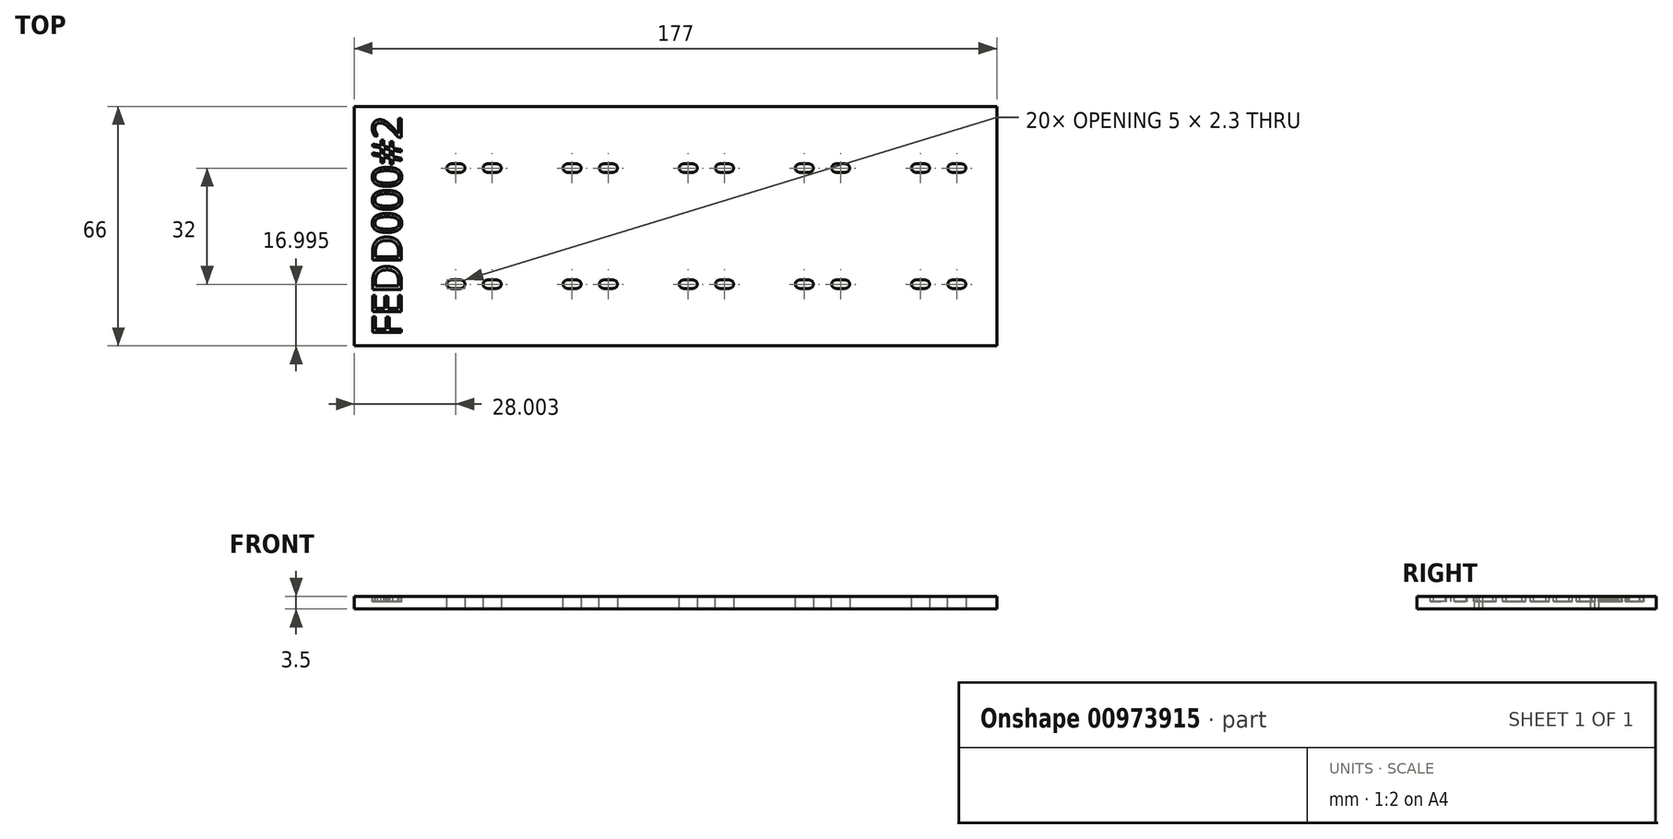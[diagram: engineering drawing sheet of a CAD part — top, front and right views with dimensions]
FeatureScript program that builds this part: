
annotation { "Feature Type Name" : "Feature", "Feature Type Description" : "" }
export const myFeature = defineFeature(function(context is Context, id is Id, definition is map)
    precondition{}
    {
        {
            var Q0;
            Q0=qCreatedBy(makeId("Top.planeOp"),FACE);
            var sketch = newSketch(context, id + "F0", { "sketchPlane" : qUnion([Q0])});
            skLineSegment(sketch, "E0.bottom", {"start": v(-87.55, 16.72) * mm, "end": v(89.45, 16.72) * mm});
            skLineSegment(sketch, "E0.top", {"start": v(-87.55, -49.28) * mm, "end": v(89.45, -49.28) * mm});
            skLineSegment(sketch, "E0.left", {"start": v(-87.55, 16.72) * mm, "end": v(-87.55, -49.28) * mm});
            skLineSegment(sketch, "E0.right", {"start": v(89.45, 16.72) * mm, "end": v(89.45, -49.28) * mm});
            skSolve(sketch);
        }
        {
            var Q0;
            Q0=makeQuery(id+"F0.imprint","IMPRINT",FACE,{"disambiguationData":[TD([[makeQuery(id+"F0.imprint","IMPRINT",EDGE,{"derivedFrom":sQuery(id+"F0.wireOp",EDGE,"E0.bottom")}),-1.0]])]});
            extrude(context, id + "F1", {"entities" : qUnion([Q0]), "depth" : 3.5 * mm, "offsetDistance" : 25 * mm});
        }
        {
            var Q0;
            Q0=makeQuery(id+"F1.opExtrude","CAP_FACE",FACE,{"disambiguationData":[OSD([sQuery(id+"F0.wireOp",EDGE,"E0.bottom"),sQuery(id+"F0.wireOp",EDGE,"E0.top"),sQuery(id+"F0.wireOp",EDGE,"E0.left"),sQuery(id+"F0.wireOp",EDGE,"E0.right")])],"isStart":false});
            var sketch = newSketch(context, id + "F2", { "sketchPlane" : qUnion([Q0])});
            skText(sketch, "E1", { "text": "FEDD000#2", "fontName": "OpenSans-Regular.ttf"});
            const initialGuessF2  = {"E1": [-0.07455, -0.0467, 0, 1, 0.008]};
            skSetInitialGuess(sketch, initialGuessF2);
            skSolve(sketch);
        }
        {
            var Q0;
            Q0=qSketchRegion(id+"F2",true);
            extrude(context, id + "F3", {"entities" : qUnion([Q0]), "operationType" : NewBodyOperationType.REMOVE, "oppositeDirection" : true, "depth" : 1.5 * mm, "offsetDistance" : 25 * mm});
        }
        {
            var Q0;
            {var subQ0=sQuery(id+"F0.wireOp",EDGE,"E0.left");var subQ1=sQuery(id+"F0.wireOp",EDGE,"E0.bottom");var subQ2=sQuery(id+"F0.wireOp",EDGE,"E0.right");var subQ3=sQuery(id+"F0.wireOp",EDGE,"E0.top");Q0=makeQuery(id+"F3.boolean.opBoolean","SPLIT",FACE,{"disambiguationData":[TD([makeQuery(id+"F1.opExtrude","SWEPT_FACE",FACE,{"disambiguationData":[OSD([subQ1])]})])],"derivedFrom":makeQuery(id+"F1.opExtrude","CAP_FACE",FACE,{"disambiguationData":[OSD([subQ1,subQ3,subQ0,subQ2])],"isStart":false})});}
            var sketch = newSketch(context, id + "F4", { "sketchPlane" : qUnion([Q0])});
            skCircle(sketch, "E2", {"center": v(-59.55, -0.28) * mm, "radius": 1.15 * mm});
            skCircle(sketch, "E3", {"center": v(-49.55, -0.28) * mm, "radius": 1.15 * mm});
            skCircle(sketch, "E4", {"center": v(-27.55, -0.28) * mm, "radius": 1.15 * mm});
            skCircle(sketch, "E5", {"center": v(-17.55, -0.28) * mm, "radius": 1.15 * mm});
            skCircle(sketch, "E6", {"center": v(4.45, -0.28) * mm, "radius": 1.15 * mm});
            skCircle(sketch, "E7", {"center": v(14.45, -0.28) * mm, "radius": 1.15 * mm});
            skCircle(sketch, "E8", {"center": v(36.45, -0.28) * mm, "radius": 1.15 * mm});
            skCircle(sketch, "E9", {"center": v(46.45, -0.28) * mm, "radius": 1.15 * mm});
            skCircle(sketch, "E10", {"center": v(68.45, -0.28) * mm, "radius": 1.15 * mm});
            skCircle(sketch, "E11", {"center": v(78.45, -0.28) * mm, "radius": 1.15 * mm});
            skCircle(sketch, "E12", {"center": v(-59.55, -32.28) * mm, "radius": 1.15 * mm});
            skCircle(sketch, "E13", {"center": v(-49.55, -32.28) * mm, "radius": 1.15 * mm});
            skCircle(sketch, "E14", {"center": v(-27.55, -32.28) * mm, "radius": 1.15 * mm});
            skCircle(sketch, "E15", {"center": v(-17.55, -32.28) * mm, "radius": 1.15 * mm});
            skCircle(sketch, "E16", {"center": v(4.45, -32.28) * mm, "radius": 1.15 * mm});
            skCircle(sketch, "E17", {"center": v(14.45, -32.28) * mm, "radius": 1.15 * mm});
            skCircle(sketch, "E18", {"center": v(36.45, -32.28) * mm, "radius": 1.15 * mm});
            skCircle(sketch, "E19", {"center": v(46.45, -32.28) * mm, "radius": 1.15 * mm});
            skCircle(sketch, "E20", {"center": v(68.45, -32.28) * mm, "radius": 1.15 * mm});
            skCircle(sketch, "E21", {"center": v(78.45, -32.28) * mm, "radius": 1.15 * mm});
            skLineSegment(sketch, "E22.bottom", {"start": v(-62.05, -31.13) * mm, "end": v(-57.05, -31.13) * mm});
            skLineSegment(sketch, "E22.top", {"start": v(-62.05, -33.43) * mm, "end": v(-57.05, -33.43) * mm});
            skLineSegment(sketch, "E22.left", {"start": v(-62.05, -31.13) * mm, "end": v(-62.05, -33.43) * mm});
            skLineSegment(sketch, "E22.right", {"start": v(-57.05, -31.13) * mm, "end": v(-57.05, -33.43) * mm});
            skLineSegment(sketch, "E23.bottom", {"start": v(-62.05, 0.87) * mm, "end": v(-57.05, 0.87) * mm});
            skLineSegment(sketch, "E23.top", {"start": v(-62.05, -1.43) * mm, "end": v(-57.05, -1.43) * mm});
            skLineSegment(sketch, "E23.left", {"start": v(-62.05, 0.87) * mm, "end": v(-62.05, -1.43) * mm});
            skLineSegment(sketch, "E23.right", {"start": v(-57.05, 0.87) * mm, "end": v(-57.05, -1.43) * mm});
            skLineSegment(sketch, "E24.bottom", {"start": v(-52.05, 0.87) * mm, "end": v(-47.05, 0.87) * mm});
            skLineSegment(sketch, "E24.top", {"start": v(-52.05, -1.43) * mm, "end": v(-47.05, -1.43) * mm});
            skLineSegment(sketch, "E24.left", {"start": v(-52.05, 0.87) * mm, "end": v(-52.05, -1.43) * mm});
            skLineSegment(sketch, "E24.right", {"start": v(-47.05, 0.87) * mm, "end": v(-47.05, -1.43) * mm});
            skLineSegment(sketch, "E25.bottom", {"start": v(-30.05, 0.87) * mm, "end": v(-25.05, 0.87) * mm});
            skLineSegment(sketch, "E25.top", {"start": v(-30.05, -1.43) * mm, "end": v(-25.05, -1.43) * mm});
            skLineSegment(sketch, "E25.left", {"start": v(-30.05, 0.87) * mm, "end": v(-30.05, -1.43) * mm});
            skLineSegment(sketch, "E25.right", {"start": v(-25.05, 0.87) * mm, "end": v(-25.05, -1.43) * mm});
            skLineSegment(sketch, "E26.bottom", {"start": v(-20.05, 0.87) * mm, "end": v(-15.05, 0.87) * mm});
            skLineSegment(sketch, "E26.top", {"start": v(-20.05, -1.43) * mm, "end": v(-15.05, -1.43) * mm});
            skLineSegment(sketch, "E26.left", {"start": v(-20.05, 0.87) * mm, "end": v(-20.05, -1.43) * mm});
            skLineSegment(sketch, "E26.right", {"start": v(-15.05, 0.87) * mm, "end": v(-15.05, -1.43) * mm});
            skLineSegment(sketch, "E27.bottom", {"start": v(1.95, 0.87) * mm, "end": v(6.95, 0.87) * mm});
            skLineSegment(sketch, "E27.top", {"start": v(1.95, -1.43) * mm, "end": v(6.95, -1.43) * mm});
            skLineSegment(sketch, "E27.left", {"start": v(1.95, 0.87) * mm, "end": v(1.95, -1.43) * mm});
            skLineSegment(sketch, "E27.right", {"start": v(6.95, 0.87) * mm, "end": v(6.95, -1.43) * mm});
            skLineSegment(sketch, "E28.bottom", {"start": v(11.95, 0.87) * mm, "end": v(16.95, 0.87) * mm});
            skLineSegment(sketch, "E28.top", {"start": v(11.95, -1.43) * mm, "end": v(16.95, -1.43) * mm});
            skLineSegment(sketch, "E28.left", {"start": v(11.95, 0.87) * mm, "end": v(11.95, -1.43) * mm});
            skLineSegment(sketch, "E28.right", {"start": v(16.95, 0.87) * mm, "end": v(16.95, -1.43) * mm});
            skLineSegment(sketch, "E29.bottom", {"start": v(33.95, 0.87) * mm, "end": v(38.95, 0.87) * mm});
            skLineSegment(sketch, "E29.top", {"start": v(33.95, -1.43) * mm, "end": v(38.95, -1.43) * mm});
            skLineSegment(sketch, "E29.left", {"start": v(33.95, 0.87) * mm, "end": v(33.95, -1.43) * mm});
            skLineSegment(sketch, "E29.right", {"start": v(38.95, 0.87) * mm, "end": v(38.95, -1.43) * mm});
            skLineSegment(sketch, "E30.bottom", {"start": v(43.95, 0.87) * mm, "end": v(48.95, 0.87) * mm});
            skLineSegment(sketch, "E30.top", {"start": v(43.95, -1.43) * mm, "end": v(48.95, -1.43) * mm});
            skLineSegment(sketch, "E30.left", {"start": v(43.95, 0.87) * mm, "end": v(43.95, -1.43) * mm});
            skLineSegment(sketch, "E30.right", {"start": v(48.95, 0.87) * mm, "end": v(48.95, -1.43) * mm});
            skLineSegment(sketch, "E31.bottom", {"start": v(65.95, 0.87) * mm, "end": v(70.95, 0.87) * mm});
            skLineSegment(sketch, "E31.top", {"start": v(65.95, -1.43) * mm, "end": v(70.95, -1.43) * mm});
            skLineSegment(sketch, "E31.left", {"start": v(65.95, 0.87) * mm, "end": v(65.95, -1.43) * mm});
            skLineSegment(sketch, "E31.right", {"start": v(70.95, 0.87) * mm, "end": v(70.95, -1.43) * mm});
            skLineSegment(sketch, "E32.bottom", {"start": v(75.95, 0.87) * mm, "end": v(80.95, 0.87) * mm});
            skLineSegment(sketch, "E32.top", {"start": v(75.95, -1.43) * mm, "end": v(80.95, -1.43) * mm});
            skLineSegment(sketch, "E32.left", {"start": v(75.95, 0.87) * mm, "end": v(75.95, -1.43) * mm});
            skLineSegment(sketch, "E32.right", {"start": v(80.95, 0.87) * mm, "end": v(80.95, -1.43) * mm});
            skLineSegment(sketch, "E33.bottom", {"start": v(-52.05, -31.13) * mm, "end": v(-47.05, -31.13) * mm});
            skLineSegment(sketch, "E33.top", {"start": v(-52.05, -33.43) * mm, "end": v(-47.05, -33.43) * mm});
            skLineSegment(sketch, "E33.left", {"start": v(-52.05, -31.13) * mm, "end": v(-52.05, -33.43) * mm});
            skLineSegment(sketch, "E33.right", {"start": v(-47.05, -31.13) * mm, "end": v(-47.05, -33.43) * mm});
            skLineSegment(sketch, "E34.bottom", {"start": v(-30.05, -31.13) * mm, "end": v(-25.05, -31.13) * mm});
            skLineSegment(sketch, "E34.top", {"start": v(-30.05, -33.43) * mm, "end": v(-25.05, -33.43) * mm});
            skLineSegment(sketch, "E34.left", {"start": v(-30.05, -31.13) * mm, "end": v(-30.05, -33.43) * mm});
            skLineSegment(sketch, "E34.right", {"start": v(-25.05, -31.13) * mm, "end": v(-25.05, -33.43) * mm});
            skLineSegment(sketch, "E35.bottom", {"start": v(-20.05, -31.13) * mm, "end": v(-15.05, -31.13) * mm});
            skLineSegment(sketch, "E35.top", {"start": v(-20.05, -33.43) * mm, "end": v(-15.05, -33.43) * mm});
            skLineSegment(sketch, "E35.left", {"start": v(-20.05, -31.13) * mm, "end": v(-20.05, -33.43) * mm});
            skLineSegment(sketch, "E35.right", {"start": v(-15.05, -31.13) * mm, "end": v(-15.05, -33.43) * mm});
            skLineSegment(sketch, "E36.bottom", {"start": v(1.95, -31.13) * mm, "end": v(6.95, -31.13) * mm});
            skLineSegment(sketch, "E36.top", {"start": v(1.95, -33.43) * mm, "end": v(6.95, -33.43) * mm});
            skLineSegment(sketch, "E36.left", {"start": v(1.95, -31.13) * mm, "end": v(1.95, -33.43) * mm});
            skLineSegment(sketch, "E36.right", {"start": v(6.95, -31.13) * mm, "end": v(6.95, -33.43) * mm});
            skLineSegment(sketch, "E37.bottom", {"start": v(11.95, -31.13) * mm, "end": v(16.95, -31.13) * mm});
            skLineSegment(sketch, "E37.top", {"start": v(11.95, -33.43) * mm, "end": v(16.95, -33.43) * mm});
            skLineSegment(sketch, "E37.left", {"start": v(11.95, -31.13) * mm, "end": v(11.95, -33.43) * mm});
            skLineSegment(sketch, "E37.right", {"start": v(16.95, -31.13) * mm, "end": v(16.95, -33.43) * mm});
            skLineSegment(sketch, "E38.bottom", {"start": v(33.95, -31.13) * mm, "end": v(38.95, -31.13) * mm});
            skLineSegment(sketch, "E38.top", {"start": v(33.95, -33.43) * mm, "end": v(38.95, -33.43) * mm});
            skLineSegment(sketch, "E38.left", {"start": v(33.95, -31.13) * mm, "end": v(33.95, -33.43) * mm});
            skLineSegment(sketch, "E38.right", {"start": v(38.95, -31.13) * mm, "end": v(38.95, -33.43) * mm});
            skLineSegment(sketch, "E39.bottom", {"start": v(43.95, -31.13) * mm, "end": v(48.95, -31.13) * mm});
            skLineSegment(sketch, "E39.top", {"start": v(43.95, -33.43) * mm, "end": v(48.95, -33.43) * mm});
            skLineSegment(sketch, "E39.left", {"start": v(43.95, -31.13) * mm, "end": v(43.95, -33.43) * mm});
            skLineSegment(sketch, "E39.right", {"start": v(48.95, -31.13) * mm, "end": v(48.95, -33.43) * mm});
            skLineSegment(sketch, "E40.bottom", {"start": v(65.95, -31.13) * mm, "end": v(70.95, -31.13) * mm});
            skLineSegment(sketch, "E40.top", {"start": v(65.95, -33.43) * mm, "end": v(70.95, -33.43) * mm});
            skLineSegment(sketch, "E40.left", {"start": v(65.95, -31.13) * mm, "end": v(65.95, -33.43) * mm});
            skLineSegment(sketch, "E40.right", {"start": v(70.95, -31.13) * mm, "end": v(70.95, -33.43) * mm});
            skLineSegment(sketch, "E41.bottom", {"start": v(75.95, -31.13) * mm, "end": v(80.95, -31.13) * mm});
            skLineSegment(sketch, "E41.top", {"start": v(75.95, -33.43) * mm, "end": v(80.95, -33.43) * mm});
            skLineSegment(sketch, "E41.left", {"start": v(75.95, -31.13) * mm, "end": v(75.95, -33.43) * mm});
            skLineSegment(sketch, "E41.right", {"start": v(80.95, -31.13) * mm, "end": v(80.95, -33.43) * mm});
            skSolve(sketch);
        }
        {
            var Q0;
            Q0=qSketchRegion(id+"F4",true);
            extrude(context, id + "F5", {"entities" : qUnion([Q0]), "operationType" : NewBodyOperationType.REMOVE, "endBound" : BoundingType.UP_TO_NEXT, "oppositeDirection" : true, "depth" : 25 * mm, "offsetDistance" : 25 * mm});
        }
        {
            var Q0;
            Q0=makeQuery(id+"F5.boolean.opBoolean","COPY",EDGE,{"derivedFrom":makeQuery(id+"F5.opExtrude","SWEPT_EDGE",EDGE,{"disambiguationData":[OSD([sQuery(id+"F4.wireOp",EDGE,"E23.bottom"),sQuery(id+"F4.wireOp",EDGE,"E23.left")])]})});
            var Q1;
            Q1=makeQuery(id+"F5.boolean.opBoolean","COPY",EDGE,{"derivedFrom":makeQuery(id+"F5.opExtrude","SWEPT_EDGE",EDGE,{"disambiguationData":[OSD([sQuery(id+"F4.wireOp",EDGE,"E24.bottom"),sQuery(id+"F4.wireOp",EDGE,"E24.left")])]})});
            var Q2;
            Q2=makeQuery(id+"F5.boolean.opBoolean","COPY",EDGE,{"derivedFrom":makeQuery(id+"F5.opExtrude","SWEPT_EDGE",EDGE,{"disambiguationData":[OSD([sQuery(id+"F4.wireOp",EDGE,"E25.bottom"),sQuery(id+"F4.wireOp",EDGE,"E25.left")])]})});
            var Q3;
            Q3=makeQuery(id+"F5.boolean.opBoolean","COPY",EDGE,{"derivedFrom":makeQuery(id+"F5.opExtrude","SWEPT_EDGE",EDGE,{"disambiguationData":[OSD([sQuery(id+"F4.wireOp",EDGE,"E26.bottom"),sQuery(id+"F4.wireOp",EDGE,"E26.left")])]})});
            var Q4;
            Q4=makeQuery(id+"F5.boolean.opBoolean","COPY",EDGE,{"derivedFrom":makeQuery(id+"F5.opExtrude","SWEPT_EDGE",EDGE,{"disambiguationData":[OSD([sQuery(id+"F4.wireOp",EDGE,"E27.bottom"),sQuery(id+"F4.wireOp",EDGE,"E27.left")])]})});
            var Q5;
            Q5=makeQuery(id+"F5.boolean.opBoolean","COPY",EDGE,{"derivedFrom":makeQuery(id+"F5.opExtrude","SWEPT_EDGE",EDGE,{"disambiguationData":[OSD([sQuery(id+"F4.wireOp",EDGE,"E28.bottom"),sQuery(id+"F4.wireOp",EDGE,"E28.left")])]})});
            var Q6;
            Q6=makeQuery(id+"F5.boolean.opBoolean","COPY",EDGE,{"derivedFrom":makeQuery(id+"F5.opExtrude","SWEPT_EDGE",EDGE,{"disambiguationData":[OSD([sQuery(id+"F4.wireOp",EDGE,"E29.bottom"),sQuery(id+"F4.wireOp",EDGE,"E29.left")])]})});
            var Q7;
            Q7=makeQuery(id+"F5.boolean.opBoolean","COPY",EDGE,{"derivedFrom":makeQuery(id+"F5.opExtrude","SWEPT_EDGE",EDGE,{"disambiguationData":[OSD([sQuery(id+"F4.wireOp",EDGE,"E30.bottom"),sQuery(id+"F4.wireOp",EDGE,"E30.left")])]})});
            var Q8;
            Q8=makeQuery(id+"F5.boolean.opBoolean","COPY",EDGE,{"derivedFrom":makeQuery(id+"F5.opExtrude","SWEPT_EDGE",EDGE,{"disambiguationData":[OSD([sQuery(id+"F4.wireOp",EDGE,"E31.bottom"),sQuery(id+"F4.wireOp",EDGE,"E31.left")])]})});
            var Q9;
            Q9=makeQuery(id+"F5.boolean.opBoolean","COPY",EDGE,{"derivedFrom":makeQuery(id+"F5.opExtrude","SWEPT_EDGE",EDGE,{"disambiguationData":[OSD([sQuery(id+"F4.wireOp",EDGE,"E32.bottom"),sQuery(id+"F4.wireOp",EDGE,"E32.left")])]})});
            var Q10;
            Q10=makeQuery(id+"F5.boolean.opBoolean","COPY",EDGE,{"derivedFrom":makeQuery(id+"F5.opExtrude","SWEPT_EDGE",EDGE,{"disambiguationData":[OSD([sQuery(id+"F4.wireOp",EDGE,"E41.bottom"),sQuery(id+"F4.wireOp",EDGE,"E41.left")])]})});
            var Q11;
            Q11=makeQuery(id+"F5.boolean.opBoolean","COPY",EDGE,{"derivedFrom":makeQuery(id+"F5.opExtrude","SWEPT_EDGE",EDGE,{"disambiguationData":[OSD([sQuery(id+"F4.wireOp",EDGE,"E40.bottom"),sQuery(id+"F4.wireOp",EDGE,"E40.left")])]})});
            var Q12;
            Q12=makeQuery(id+"F5.boolean.opBoolean","COPY",EDGE,{"derivedFrom":makeQuery(id+"F5.opExtrude","SWEPT_EDGE",EDGE,{"disambiguationData":[OSD([sQuery(id+"F4.wireOp",EDGE,"E39.bottom"),sQuery(id+"F4.wireOp",EDGE,"E39.left")])]})});
            var Q13;
            Q13=makeQuery(id+"F5.boolean.opBoolean","COPY",EDGE,{"derivedFrom":makeQuery(id+"F5.opExtrude","SWEPT_EDGE",EDGE,{"disambiguationData":[OSD([sQuery(id+"F4.wireOp",EDGE,"E34.bottom"),sQuery(id+"F4.wireOp",EDGE,"E34.left")])]})});
            var Q14;
            Q14=makeQuery(id+"F5.boolean.opBoolean","COPY",EDGE,{"derivedFrom":makeQuery(id+"F5.opExtrude","SWEPT_EDGE",EDGE,{"disambiguationData":[OSD([sQuery(id+"F4.wireOp",EDGE,"E35.bottom"),sQuery(id+"F4.wireOp",EDGE,"E35.left")])]})});
            var Q15;
            Q15=makeQuery(id+"F5.boolean.opBoolean","COPY",EDGE,{"derivedFrom":makeQuery(id+"F5.opExtrude","SWEPT_EDGE",EDGE,{"disambiguationData":[OSD([sQuery(id+"F4.wireOp",EDGE,"E36.bottom"),sQuery(id+"F4.wireOp",EDGE,"E36.left")])]})});
            var Q16;
            Q16=makeQuery(id+"F5.boolean.opBoolean","COPY",EDGE,{"derivedFrom":makeQuery(id+"F5.opExtrude","SWEPT_EDGE",EDGE,{"disambiguationData":[OSD([sQuery(id+"F4.wireOp",EDGE,"E37.bottom"),sQuery(id+"F4.wireOp",EDGE,"E37.left")])]})});
            var Q17;
            Q17=makeQuery(id+"F5.boolean.opBoolean","COPY",EDGE,{"derivedFrom":makeQuery(id+"F5.opExtrude","SWEPT_EDGE",EDGE,{"disambiguationData":[OSD([sQuery(id+"F4.wireOp",EDGE,"E38.bottom"),sQuery(id+"F4.wireOp",EDGE,"E38.left")])]})});
            var Q18;
            Q18=makeQuery(id+"F5.boolean.opBoolean","COPY",EDGE,{"derivedFrom":makeQuery(id+"F5.opExtrude","SWEPT_EDGE",EDGE,{"disambiguationData":[OSD([sQuery(id+"F4.wireOp",EDGE,"E22.bottom"),sQuery(id+"F4.wireOp",EDGE,"E22.left")])]})});
            var Q19;
            Q19=makeQuery(id+"F5.boolean.opBoolean","COPY",EDGE,{"derivedFrom":makeQuery(id+"F5.opExtrude","SWEPT_EDGE",EDGE,{"disambiguationData":[OSD([sQuery(id+"F4.wireOp",EDGE,"E33.bottom"),sQuery(id+"F4.wireOp",EDGE,"E33.left")])]})});
            var Q20;
            Q20=makeQuery(id+"F5.boolean.opBoolean","COPY",EDGE,{"derivedFrom":makeQuery(id+"F5.opExtrude","SWEPT_EDGE",EDGE,{"disambiguationData":[OSD([sQuery(id+"F4.wireOp",EDGE,"E23.bottom"),sQuery(id+"F4.wireOp",EDGE,"E23.right")])]})});
            var Q21;
            Q21=makeQuery(id+"F5.boolean.opBoolean","COPY",EDGE,{"derivedFrom":makeQuery(id+"F5.opExtrude","SWEPT_EDGE",EDGE,{"disambiguationData":[OSD([sQuery(id+"F4.wireOp",EDGE,"E24.bottom"),sQuery(id+"F4.wireOp",EDGE,"E24.right")])]})});
            var Q22;
            Q22=makeQuery(id+"F5.boolean.opBoolean","COPY",EDGE,{"derivedFrom":makeQuery(id+"F5.opExtrude","SWEPT_EDGE",EDGE,{"disambiguationData":[OSD([sQuery(id+"F4.wireOp",EDGE,"E25.bottom"),sQuery(id+"F4.wireOp",EDGE,"E25.right")])]})});
            var Q23;
            Q23=makeQuery(id+"F5.boolean.opBoolean","COPY",EDGE,{"derivedFrom":makeQuery(id+"F5.opExtrude","SWEPT_EDGE",EDGE,{"disambiguationData":[OSD([sQuery(id+"F4.wireOp",EDGE,"E26.bottom"),sQuery(id+"F4.wireOp",EDGE,"E26.right")])]})});
            var Q24;
            Q24=makeQuery(id+"F5.boolean.opBoolean","COPY",EDGE,{"derivedFrom":makeQuery(id+"F5.opExtrude","SWEPT_EDGE",EDGE,{"disambiguationData":[OSD([sQuery(id+"F4.wireOp",EDGE,"E27.bottom"),sQuery(id+"F4.wireOp",EDGE,"E27.right")])]})});
            var Q25;
            Q25=makeQuery(id+"F5.boolean.opBoolean","COPY",EDGE,{"derivedFrom":makeQuery(id+"F5.opExtrude","SWEPT_EDGE",EDGE,{"disambiguationData":[OSD([sQuery(id+"F4.wireOp",EDGE,"E28.bottom"),sQuery(id+"F4.wireOp",EDGE,"E28.right")])]})});
            var Q26;
            Q26=makeQuery(id+"F5.boolean.opBoolean","COPY",EDGE,{"derivedFrom":makeQuery(id+"F5.opExtrude","SWEPT_EDGE",EDGE,{"disambiguationData":[OSD([sQuery(id+"F4.wireOp",EDGE,"E29.bottom"),sQuery(id+"F4.wireOp",EDGE,"E29.right")])]})});
            var Q27;
            Q27=makeQuery(id+"F5.boolean.opBoolean","COPY",EDGE,{"derivedFrom":makeQuery(id+"F5.opExtrude","SWEPT_EDGE",EDGE,{"disambiguationData":[OSD([sQuery(id+"F4.wireOp",EDGE,"E30.bottom"),sQuery(id+"F4.wireOp",EDGE,"E30.right")])]})});
            var Q28;
            Q28=makeQuery(id+"F5.boolean.opBoolean","COPY",EDGE,{"derivedFrom":makeQuery(id+"F5.opExtrude","SWEPT_EDGE",EDGE,{"disambiguationData":[OSD([sQuery(id+"F4.wireOp",EDGE,"E31.bottom"),sQuery(id+"F4.wireOp",EDGE,"E31.right")])]})});
            var Q29;
            Q29=makeQuery(id+"F5.boolean.opBoolean","COPY",EDGE,{"derivedFrom":makeQuery(id+"F5.opExtrude","SWEPT_EDGE",EDGE,{"disambiguationData":[OSD([sQuery(id+"F4.wireOp",EDGE,"E32.bottom"),sQuery(id+"F4.wireOp",EDGE,"E32.right")])]})});
            var Q30;
            Q30=makeQuery(id+"F5.boolean.opBoolean","COPY",EDGE,{"derivedFrom":makeQuery(id+"F5.opExtrude","SWEPT_EDGE",EDGE,{"disambiguationData":[OSD([sQuery(id+"F4.wireOp",EDGE,"E41.bottom"),sQuery(id+"F4.wireOp",EDGE,"E41.right")])]})});
            var Q31;
            Q31=makeQuery(id+"F5.boolean.opBoolean","COPY",EDGE,{"derivedFrom":makeQuery(id+"F5.opExtrude","SWEPT_EDGE",EDGE,{"disambiguationData":[OSD([sQuery(id+"F4.wireOp",EDGE,"E40.bottom"),sQuery(id+"F4.wireOp",EDGE,"E40.right")])]})});
            var Q32;
            Q32=makeQuery(id+"F5.boolean.opBoolean","COPY",EDGE,{"derivedFrom":makeQuery(id+"F5.opExtrude","SWEPT_EDGE",EDGE,{"disambiguationData":[OSD([sQuery(id+"F4.wireOp",EDGE,"E39.bottom"),sQuery(id+"F4.wireOp",EDGE,"E39.right")])]})});
            var Q33;
            Q33=makeQuery(id+"F5.boolean.opBoolean","COPY",EDGE,{"derivedFrom":makeQuery(id+"F5.opExtrude","SWEPT_EDGE",EDGE,{"disambiguationData":[OSD([sQuery(id+"F4.wireOp",EDGE,"E38.bottom"),sQuery(id+"F4.wireOp",EDGE,"E38.right")])]})});
            var Q34;
            Q34=makeQuery(id+"F5.boolean.opBoolean","COPY",EDGE,{"derivedFrom":makeQuery(id+"F5.opExtrude","SWEPT_EDGE",EDGE,{"disambiguationData":[OSD([sQuery(id+"F4.wireOp",EDGE,"E37.bottom"),sQuery(id+"F4.wireOp",EDGE,"E37.right")])]})});
            var Q35;
            Q35=makeQuery(id+"F5.boolean.opBoolean","COPY",EDGE,{"derivedFrom":makeQuery(id+"F5.opExtrude","SWEPT_EDGE",EDGE,{"disambiguationData":[OSD([sQuery(id+"F4.wireOp",EDGE,"E36.bottom"),sQuery(id+"F4.wireOp",EDGE,"E36.right")])]})});
            var Q36;
            Q36=makeQuery(id+"F5.boolean.opBoolean","COPY",EDGE,{"derivedFrom":makeQuery(id+"F5.opExtrude","SWEPT_EDGE",EDGE,{"disambiguationData":[OSD([sQuery(id+"F4.wireOp",EDGE,"E35.bottom"),sQuery(id+"F4.wireOp",EDGE,"E35.right")])]})});
            var Q37;
            Q37=makeQuery(id+"F5.boolean.opBoolean","COPY",EDGE,{"derivedFrom":makeQuery(id+"F5.opExtrude","SWEPT_EDGE",EDGE,{"disambiguationData":[OSD([sQuery(id+"F4.wireOp",EDGE,"E34.bottom"),sQuery(id+"F4.wireOp",EDGE,"E34.right")])]})});
            var Q38;
            Q38=makeQuery(id+"F5.boolean.opBoolean","COPY",EDGE,{"derivedFrom":makeQuery(id+"F5.opExtrude","SWEPT_EDGE",EDGE,{"disambiguationData":[OSD([sQuery(id+"F4.wireOp",EDGE,"E33.bottom"),sQuery(id+"F4.wireOp",EDGE,"E33.right")])]})});
            var Q39;
            Q39=makeQuery(id+"F5.boolean.opBoolean","COPY",EDGE,{"derivedFrom":makeQuery(id+"F5.opExtrude","SWEPT_EDGE",EDGE,{"disambiguationData":[OSD([sQuery(id+"F4.wireOp",EDGE,"E22.bottom"),sQuery(id+"F4.wireOp",EDGE,"E22.right")])]})});
            var Q40;
            Q40=makeQuery(id+"F5.boolean.opBoolean","COPY",EDGE,{"derivedFrom":makeQuery(id+"F5.opExtrude","SWEPT_EDGE",EDGE,{"disambiguationData":[OSD([sQuery(id+"F4.wireOp",EDGE,"E32.top"),sQuery(id+"F4.wireOp",EDGE,"E32.right")])]})});
            var Q41;
            Q41=makeQuery(id+"F5.boolean.opBoolean","COPY",EDGE,{"derivedFrom":makeQuery(id+"F5.opExtrude","SWEPT_EDGE",EDGE,{"disambiguationData":[OSD([sQuery(id+"F4.wireOp",EDGE,"E41.top"),sQuery(id+"F4.wireOp",EDGE,"E41.right")])]})});
            var Q42;
            Q42=makeQuery(id+"F5.boolean.opBoolean","COPY",EDGE,{"derivedFrom":makeQuery(id+"F5.opExtrude","SWEPT_EDGE",EDGE,{"disambiguationData":[OSD([sQuery(id+"F4.wireOp",EDGE,"E31.top"),sQuery(id+"F4.wireOp",EDGE,"E31.right")])]})});
            var Q43;
            Q43=makeQuery(id+"F5.boolean.opBoolean","COPY",EDGE,{"derivedFrom":makeQuery(id+"F5.opExtrude","SWEPT_EDGE",EDGE,{"disambiguationData":[OSD([sQuery(id+"F4.wireOp",EDGE,"E30.top"),sQuery(id+"F4.wireOp",EDGE,"E30.right")])]})});
            var Q44;
            Q44=makeQuery(id+"F5.boolean.opBoolean","COPY",EDGE,{"derivedFrom":makeQuery(id+"F5.opExtrude","SWEPT_EDGE",EDGE,{"disambiguationData":[OSD([sQuery(id+"F4.wireOp",EDGE,"E39.top"),sQuery(id+"F4.wireOp",EDGE,"E39.right")])]})});
            var Q45;
            Q45=makeQuery(id+"F5.boolean.opBoolean","COPY",EDGE,{"derivedFrom":makeQuery(id+"F5.opExtrude","SWEPT_EDGE",EDGE,{"disambiguationData":[OSD([sQuery(id+"F4.wireOp",EDGE,"E38.top"),sQuery(id+"F4.wireOp",EDGE,"E38.right")])]})});
            var Q46;
            Q46=makeQuery(id+"F5.boolean.opBoolean","COPY",EDGE,{"derivedFrom":makeQuery(id+"F5.opExtrude","SWEPT_EDGE",EDGE,{"disambiguationData":[OSD([sQuery(id+"F4.wireOp",EDGE,"E29.top"),sQuery(id+"F4.wireOp",EDGE,"E29.right")])]})});
            var Q47;
            Q47=makeQuery(id+"F5.boolean.opBoolean","COPY",EDGE,{"derivedFrom":makeQuery(id+"F5.opExtrude","SWEPT_EDGE",EDGE,{"disambiguationData":[OSD([sQuery(id+"F4.wireOp",EDGE,"E28.top"),sQuery(id+"F4.wireOp",EDGE,"E28.right")])]})});
            var Q48;
            Q48=makeQuery(id+"F5.boolean.opBoolean","COPY",EDGE,{"derivedFrom":makeQuery(id+"F5.opExtrude","SWEPT_EDGE",EDGE,{"disambiguationData":[OSD([sQuery(id+"F4.wireOp",EDGE,"E27.top"),sQuery(id+"F4.wireOp",EDGE,"E27.right")])]})});
            var Q49;
            Q49=makeQuery(id+"F5.boolean.opBoolean","COPY",EDGE,{"derivedFrom":makeQuery(id+"F5.opExtrude","SWEPT_EDGE",EDGE,{"disambiguationData":[OSD([sQuery(id+"F4.wireOp",EDGE,"E26.top"),sQuery(id+"F4.wireOp",EDGE,"E26.right")])]})});
            var Q50;
            Q50=makeQuery(id+"F5.boolean.opBoolean","COPY",EDGE,{"derivedFrom":makeQuery(id+"F5.opExtrude","SWEPT_EDGE",EDGE,{"disambiguationData":[OSD([sQuery(id+"F4.wireOp",EDGE,"E25.top"),sQuery(id+"F4.wireOp",EDGE,"E25.right")])]})});
            var Q51;
            Q51=makeQuery(id+"F5.boolean.opBoolean","COPY",EDGE,{"derivedFrom":makeQuery(id+"F5.opExtrude","SWEPT_EDGE",EDGE,{"disambiguationData":[OSD([sQuery(id+"F4.wireOp",EDGE,"E37.top"),sQuery(id+"F4.wireOp",EDGE,"E37.right")])]})});
            var Q52;
            Q52=makeQuery(id+"F5.boolean.opBoolean","COPY",EDGE,{"derivedFrom":makeQuery(id+"F5.opExtrude","SWEPT_EDGE",EDGE,{"disambiguationData":[OSD([sQuery(id+"F4.wireOp",EDGE,"E36.top"),sQuery(id+"F4.wireOp",EDGE,"E36.right")])]})});
            var Q53;
            Q53=makeQuery(id+"F5.boolean.opBoolean","COPY",EDGE,{"derivedFrom":makeQuery(id+"F5.opExtrude","SWEPT_EDGE",EDGE,{"disambiguationData":[OSD([sQuery(id+"F4.wireOp",EDGE,"E35.top"),sQuery(id+"F4.wireOp",EDGE,"E35.right")])]})});
            var Q54;
            Q54=makeQuery(id+"F5.boolean.opBoolean","COPY",EDGE,{"derivedFrom":makeQuery(id+"F5.opExtrude","SWEPT_EDGE",EDGE,{"disambiguationData":[OSD([sQuery(id+"F4.wireOp",EDGE,"E34.top"),sQuery(id+"F4.wireOp",EDGE,"E34.right")])]})});
            var Q55;
            Q55=makeQuery(id+"F5.boolean.opBoolean","COPY",EDGE,{"derivedFrom":makeQuery(id+"F5.opExtrude","SWEPT_EDGE",EDGE,{"disambiguationData":[OSD([sQuery(id+"F4.wireOp",EDGE,"E33.top"),sQuery(id+"F4.wireOp",EDGE,"E33.right")])]})});
            var Q56;
            Q56=makeQuery(id+"F5.boolean.opBoolean","COPY",EDGE,{"derivedFrom":makeQuery(id+"F5.opExtrude","SWEPT_EDGE",EDGE,{"disambiguationData":[OSD([sQuery(id+"F4.wireOp",EDGE,"E22.top"),sQuery(id+"F4.wireOp",EDGE,"E22.right")])]})});
            var Q57;
            Q57=makeQuery(id+"F5.boolean.opBoolean","COPY",EDGE,{"derivedFrom":makeQuery(id+"F5.opExtrude","SWEPT_EDGE",EDGE,{"disambiguationData":[OSD([sQuery(id+"F4.wireOp",EDGE,"E23.top"),sQuery(id+"F4.wireOp",EDGE,"E23.right")])]})});
            var Q58;
            Q58=makeQuery(id+"F5.boolean.opBoolean","COPY",EDGE,{"derivedFrom":makeQuery(id+"F5.opExtrude","SWEPT_EDGE",EDGE,{"disambiguationData":[OSD([sQuery(id+"F4.wireOp",EDGE,"E24.top"),sQuery(id+"F4.wireOp",EDGE,"E24.right")])]})});
            var Q59;
            Q59=makeQuery(id+"F5.boolean.opBoolean","COPY",EDGE,{"derivedFrom":makeQuery(id+"F5.opExtrude","SWEPT_EDGE",EDGE,{"disambiguationData":[OSD([sQuery(id+"F4.wireOp",EDGE,"E41.top"),sQuery(id+"F4.wireOp",EDGE,"E41.left")])]})});
            var Q60;
            Q60=makeQuery(id+"F5.boolean.opBoolean","COPY",EDGE,{"derivedFrom":makeQuery(id+"F5.opExtrude","SWEPT_EDGE",EDGE,{"disambiguationData":[OSD([sQuery(id+"F4.wireOp",EDGE,"E40.top"),sQuery(id+"F4.wireOp",EDGE,"E40.left")])]})});
            var Q61;
            Q61=makeQuery(id+"F5.boolean.opBoolean","COPY",EDGE,{"derivedFrom":makeQuery(id+"F5.opExtrude","SWEPT_EDGE",EDGE,{"disambiguationData":[OSD([sQuery(id+"F4.wireOp",EDGE,"E32.top"),sQuery(id+"F4.wireOp",EDGE,"E32.left")])]})});
            var Q62;
            Q62=makeQuery(id+"F5.boolean.opBoolean","COPY",EDGE,{"derivedFrom":makeQuery(id+"F5.opExtrude","SWEPT_EDGE",EDGE,{"disambiguationData":[OSD([sQuery(id+"F4.wireOp",EDGE,"E31.top"),sQuery(id+"F4.wireOp",EDGE,"E31.left")])]})});
            var Q63;
            Q63=makeQuery(id+"F5.boolean.opBoolean","COPY",EDGE,{"derivedFrom":makeQuery(id+"F5.opExtrude","SWEPT_EDGE",EDGE,{"disambiguationData":[OSD([sQuery(id+"F4.wireOp",EDGE,"E30.top"),sQuery(id+"F4.wireOp",EDGE,"E30.left")])]})});
            var Q64;
            Q64=makeQuery(id+"F5.boolean.opBoolean","COPY",EDGE,{"derivedFrom":makeQuery(id+"F5.opExtrude","SWEPT_EDGE",EDGE,{"disambiguationData":[OSD([sQuery(id+"F4.wireOp",EDGE,"E29.top"),sQuery(id+"F4.wireOp",EDGE,"E29.left")])]})});
            var Q65;
            Q65=makeQuery(id+"F5.boolean.opBoolean","COPY",EDGE,{"derivedFrom":makeQuery(id+"F5.opExtrude","SWEPT_EDGE",EDGE,{"disambiguationData":[OSD([sQuery(id+"F4.wireOp",EDGE,"E28.top"),sQuery(id+"F4.wireOp",EDGE,"E28.left")])]})});
            var Q66;
            Q66=makeQuery(id+"F5.boolean.opBoolean","COPY",EDGE,{"derivedFrom":makeQuery(id+"F5.opExtrude","SWEPT_EDGE",EDGE,{"disambiguationData":[OSD([sQuery(id+"F4.wireOp",EDGE,"E27.top"),sQuery(id+"F4.wireOp",EDGE,"E27.left")])]})});
            var Q67;
            Q67=makeQuery(id+"F5.boolean.opBoolean","COPY",EDGE,{"derivedFrom":makeQuery(id+"F5.opExtrude","SWEPT_EDGE",EDGE,{"disambiguationData":[OSD([sQuery(id+"F4.wireOp",EDGE,"E26.top"),sQuery(id+"F4.wireOp",EDGE,"E26.left")])]})});
            var Q68;
            Q68=makeQuery(id+"F5.boolean.opBoolean","COPY",EDGE,{"derivedFrom":makeQuery(id+"F5.opExtrude","SWEPT_EDGE",EDGE,{"disambiguationData":[OSD([sQuery(id+"F4.wireOp",EDGE,"E25.top"),sQuery(id+"F4.wireOp",EDGE,"E25.left")])]})});
            var Q69;
            Q69=makeQuery(id+"F5.boolean.opBoolean","COPY",EDGE,{"derivedFrom":makeQuery(id+"F5.opExtrude","SWEPT_EDGE",EDGE,{"disambiguationData":[OSD([sQuery(id+"F4.wireOp",EDGE,"E24.top"),sQuery(id+"F4.wireOp",EDGE,"E24.left")])]})});
            var Q70;
            Q70=makeQuery(id+"F5.boolean.opBoolean","COPY",EDGE,{"derivedFrom":makeQuery(id+"F5.opExtrude","SWEPT_EDGE",EDGE,{"disambiguationData":[OSD([sQuery(id+"F4.wireOp",EDGE,"E23.top"),sQuery(id+"F4.wireOp",EDGE,"E23.left")])]})});
            var Q71;
            Q71=makeQuery(id+"F5.boolean.opBoolean","COPY",EDGE,{"derivedFrom":makeQuery(id+"F5.opExtrude","SWEPT_EDGE",EDGE,{"disambiguationData":[OSD([sQuery(id+"F4.wireOp",EDGE,"E22.top"),sQuery(id+"F4.wireOp",EDGE,"E22.left")])]})});
            var Q72;
            Q72=makeQuery(id+"F5.boolean.opBoolean","COPY",EDGE,{"derivedFrom":makeQuery(id+"F5.opExtrude","SWEPT_EDGE",EDGE,{"disambiguationData":[OSD([sQuery(id+"F4.wireOp",EDGE,"E33.top"),sQuery(id+"F4.wireOp",EDGE,"E33.left")])]})});
            var Q73;
            Q73=makeQuery(id+"F5.boolean.opBoolean","COPY",EDGE,{"derivedFrom":makeQuery(id+"F5.opExtrude","SWEPT_EDGE",EDGE,{"disambiguationData":[OSD([sQuery(id+"F4.wireOp",EDGE,"E34.top"),sQuery(id+"F4.wireOp",EDGE,"E34.left")])]})});
            var Q74;
            Q74=makeQuery(id+"F5.boolean.opBoolean","COPY",EDGE,{"derivedFrom":makeQuery(id+"F5.opExtrude","SWEPT_EDGE",EDGE,{"disambiguationData":[OSD([sQuery(id+"F4.wireOp",EDGE,"E35.top"),sQuery(id+"F4.wireOp",EDGE,"E35.left")])]})});
            var Q75;
            Q75=makeQuery(id+"F5.boolean.opBoolean","COPY",EDGE,{"derivedFrom":makeQuery(id+"F5.opExtrude","SWEPT_EDGE",EDGE,{"disambiguationData":[OSD([sQuery(id+"F4.wireOp",EDGE,"E36.top"),sQuery(id+"F4.wireOp",EDGE,"E36.left")])]})});
            var Q76;
            Q76=makeQuery(id+"F5.boolean.opBoolean","COPY",EDGE,{"derivedFrom":makeQuery(id+"F5.opExtrude","SWEPT_EDGE",EDGE,{"disambiguationData":[OSD([sQuery(id+"F4.wireOp",EDGE,"E37.top"),sQuery(id+"F4.wireOp",EDGE,"E37.left")])]})});
            var Q77;
            Q77=makeQuery(id+"F5.boolean.opBoolean","COPY",EDGE,{"derivedFrom":makeQuery(id+"F5.opExtrude","SWEPT_EDGE",EDGE,{"disambiguationData":[OSD([sQuery(id+"F4.wireOp",EDGE,"E38.top"),sQuery(id+"F4.wireOp",EDGE,"E38.left")])]})});
            var Q78;
            Q78=makeQuery(id+"F5.boolean.opBoolean","COPY",EDGE,{"derivedFrom":makeQuery(id+"F5.opExtrude","SWEPT_EDGE",EDGE,{"disambiguationData":[OSD([sQuery(id+"F4.wireOp",EDGE,"E39.top"),sQuery(id+"F4.wireOp",EDGE,"E39.left")])]})});
            var Q79;
            Q79=makeQuery(id+"F5.boolean.opBoolean","COPY",EDGE,{"derivedFrom":makeQuery(id+"F5.opExtrude","SWEPT_EDGE",EDGE,{"disambiguationData":[OSD([sQuery(id+"F4.wireOp",EDGE,"E40.top"),sQuery(id+"F4.wireOp",EDGE,"E40.right")])]})});
            fillet(context, id + "F6", {"entities" : qUnion([Q0, Q1, Q2, Q3, Q4, Q5, Q6, Q7, Q8, Q9, Q10, Q11, Q12, Q13, Q14, Q15, Q16, Q17, Q18, Q19, Q20, Q21, Q22, Q23, Q24, Q25, Q26, Q27, Q28, Q29, Q30, Q31, Q32, Q33, Q34, Q35, Q36, Q37, Q38, Q39, Q40, Q41, Q42, Q43, Q44, Q45, Q46, Q47, Q48, Q49, Q50, Q51, Q52, Q53, Q54, Q55, Q56, Q57, Q58, Q59, Q60, Q61, Q62, Q63, Q64, Q65, Q66, Q67, Q68, Q69, Q70, Q71, Q72, Q73, Q74, Q75, Q76, Q77, Q78, Q79]), "radius" : 1.2 * mm, "tangentPropagation" : true, "allowEdgeOverflow" : false});
        }
    });
